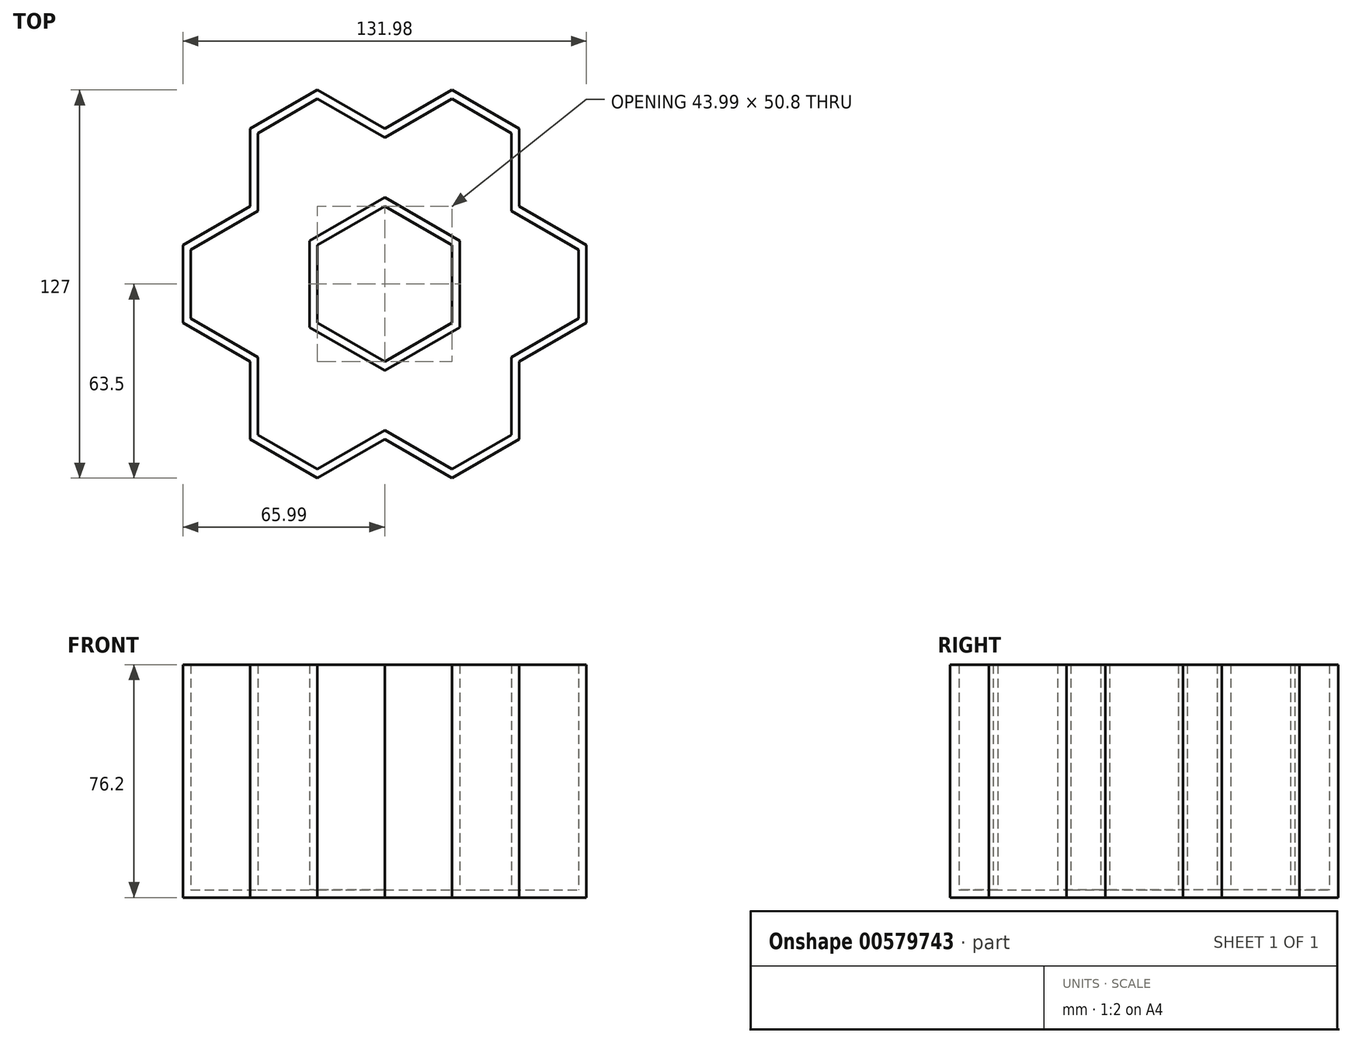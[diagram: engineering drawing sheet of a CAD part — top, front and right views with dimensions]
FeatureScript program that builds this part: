
annotation { "Feature Type Name" : "Feature", "Feature Type Description" : "" }
export const myFeature = defineFeature(function(context is Context, id is Id, definition is map)
    precondition{}
    {
        {
            var Q0;
            Q0=qCreatedBy(makeId("Top.planeOp"),FACE);
            var sketch = newSketch(context, id + "F0", { "sketchPlane" : qUnion([Q0])});
            skCircle(sketch, "E0.cCircle", {"center": v(0, 0) * mm, "radius": 25.4 * mm, "construction": true});
            skLineSegment(sketch, "E0.0", {"start": v(22, 12.7) * mm, "end": v(22, -12.7) * mm});
            skLineSegment(sketch, "E0.1", {"start": v(22, -12.7) * mm, "end": v(0, -25.4) * mm});
            skLineSegment(sketch, "E0.2", {"start": v(0, -25.4) * mm, "end": v(-22, -12.7) * mm});
            skLineSegment(sketch, "E0.3", {"start": v(-22, -12.7) * mm, "end": v(-22, 12.7) * mm});
            skLineSegment(sketch, "E0.4", {"start": v(-22, 12.7) * mm, "end": v(0, 25.4) * mm});
            skLineSegment(sketch, "E0.5", {"start": v(0, 25.4) * mm, "end": v(22, 12.7) * mm});
            skCircle(sketch, "E1.cCircle", {"center": v(44, 0) * mm, "radius": 25.4 * mm, "construction": true});
            skLineSegment(sketch, "E1.0", {"start": v(22, -12.7) * mm, "end": v(22, 12.7) * mm});
            skLineSegment(sketch, "E1.1", {"start": v(22, 12.7) * mm, "end": v(44, 25.4) * mm});
            skLineSegment(sketch, "E1.2", {"start": v(44, 25.4) * mm, "end": v(66, 12.7) * mm});
            skLineSegment(sketch, "E1.3", {"start": v(66, 12.7) * mm, "end": v(66, -12.7) * mm});
            skLineSegment(sketch, "E1.4", {"start": v(66, -12.7) * mm, "end": v(44, -25.4) * mm});
            skLineSegment(sketch, "E1.5", {"start": v(44, -25.4) * mm, "end": v(22, -12.7) * mm});
            skCircle(sketch, "E2.cCircle", {"center": v(-44, 0) * mm, "radius": 25.4 * mm, "construction": true});
            skLineSegment(sketch, "E2.0", {"start": v(-22, -12.7) * mm, "end": v(-44, -25.4) * mm});
            skLineSegment(sketch, "E2.1", {"start": v(-44, -25.4) * mm, "end": v(-66, -12.7) * mm});
            skLineSegment(sketch, "E2.2", {"start": v(-66, -12.7) * mm, "end": v(-66, 12.7) * mm});
            skLineSegment(sketch, "E2.3", {"start": v(-66, 12.7) * mm, "end": v(-44, 25.4) * mm});
            skLineSegment(sketch, "E2.4", {"start": v(-44, 25.4) * mm, "end": v(-22, 12.7) * mm});
            skLineSegment(sketch, "E2.5", {"start": v(-22, 12.7) * mm, "end": v(-22, -12.7) * mm});
            skCircle(sketch, "E3.cCircle", {"center": v(-22, 38.1) * mm, "radius": 25.4 * mm, "construction": true});
            skLineSegment(sketch, "E3.0", {"start": v(-22, 12.7) * mm, "end": v(-44, 25.4) * mm});
            skLineSegment(sketch, "E3.1", {"start": v(-44, 25.4) * mm, "end": v(-44, 50.8) * mm});
            skLineSegment(sketch, "E3.2", {"start": v(-44, 50.8) * mm, "end": v(-22, 63.5) * mm});
            skLineSegment(sketch, "E3.3", {"start": v(-22, 63.5) * mm, "end": v(0, 50.8) * mm});
            skLineSegment(sketch, "E3.4", {"start": v(0, 50.8) * mm, "end": v(0, 25.4) * mm});
            skLineSegment(sketch, "E3.5", {"start": v(0, 25.4) * mm, "end": v(-22, 12.7) * mm});
            skCircle(sketch, "E4.cCircle", {"center": v(22, 38.1) * mm, "radius": 25.4 * mm, "construction": true});
            skPoint(sketch, "E4.cCircle.centerSnap0", {"position": v(22, 0) * mm});
            skLineSegment(sketch, "E4.0", {"start": v(44, 50.8) * mm, "end": v(44, 25.4) * mm});
            skLineSegment(sketch, "E4.1", {"start": v(44, 25.4) * mm, "end": v(22, 12.7) * mm});
            skLineSegment(sketch, "E4.2", {"start": v(22, 12.7) * mm, "end": v(0, 25.4) * mm});
            skLineSegment(sketch, "E4.3", {"start": v(0, 25.4) * mm, "end": v(0, 50.8) * mm});
            skLineSegment(sketch, "E4.4", {"start": v(0, 50.8) * mm, "end": v(22, 63.5) * mm});
            skLineSegment(sketch, "E4.5", {"start": v(22, 63.5) * mm, "end": v(44, 50.8) * mm});
            skCircle(sketch, "E5.cCircle", {"center": v(-22, -38.1) * mm, "radius": 25.4 * mm, "construction": true});
            skLineSegment(sketch, "E5.0", {"start": v(0, -25.4) * mm, "end": v(0, -50.8) * mm});
            skLineSegment(sketch, "E5.1", {"start": v(0, -50.8) * mm, "end": v(-22, -63.5) * mm});
            skLineSegment(sketch, "E5.2", {"start": v(-22, -63.5) * mm, "end": v(-44, -50.8) * mm});
            skLineSegment(sketch, "E5.3", {"start": v(-44, -50.8) * mm, "end": v(-44, -25.4) * mm});
            skLineSegment(sketch, "E5.4", {"start": v(-44, -25.4) * mm, "end": v(-22, -12.7) * mm});
            skLineSegment(sketch, "E5.5", {"start": v(-22, -12.7) * mm, "end": v(0, -25.4) * mm});
            skCircle(sketch, "E6.cCircle", {"center": v(22, -38.1) * mm, "radius": 25.4 * mm, "construction": true});
            skPoint(sketch, "E6.cCircle.centerSnap0", {"position": v(0, -38.1) * mm});
            skLineSegment(sketch, "E6.0", {"start": v(44, -25.4) * mm, "end": v(44, -50.8) * mm});
            skLineSegment(sketch, "E6.1", {"start": v(44, -50.8) * mm, "end": v(22, -63.5) * mm});
            skLineSegment(sketch, "E6.2", {"start": v(22, -63.5) * mm, "end": v(0, -50.8) * mm});
            skLineSegment(sketch, "E6.3", {"start": v(0, -50.8) * mm, "end": v(0, -25.4) * mm});
            skLineSegment(sketch, "E6.4", {"start": v(0, -25.4) * mm, "end": v(22, -12.7) * mm});
            skLineSegment(sketch, "E6.5", {"start": v(22, -12.7) * mm, "end": v(44, -25.4) * mm});
            skSolve(sketch);
        }
        {
            var Q0;
            Q0 = qSketchRegion(id + "F0", true);
            var Q1;
            Q1=makeQuery(id+"F0.imprint","IMPRINT",FACE,{"disambiguationData":[TD([[makeQuery(id+"F0.imprint","IMPRINT",EDGE,{"derivedFrom":sQuery(id+"F0.wireOp",EDGE,"E1.0")}),1.0]])]});
            extrude(context, id + "F1", {"entities" : qUnion([Q0, Q1]), "depth" : 76.2 * mm, "offsetDistance" : 25.4 * mm});
        }
        {
            var Q0;
            Q0=makeQuery(id+"F1.opExtrude","CAP_FACE",FACE,{"disambiguationData":[OSD([sQuery(id+"F0.wireOp",EDGE,"E1.2"),sQuery(id+"F0.wireOp",EDGE,"E1.3"),sQuery(id+"F0.wireOp",EDGE,"E1.4"),sQuery(id+"F0.wireOp",EDGE,"E2.1"),sQuery(id+"F0.wireOp",EDGE,"E2.2"),sQuery(id+"F0.wireOp",EDGE,"E2.3"),sQuery(id+"F0.wireOp",EDGE,"E3.1"),sQuery(id+"F0.wireOp",EDGE,"E3.2"),sQuery(id+"F0.wireOp",EDGE,"E3.3"),sQuery(id+"F0.wireOp",EDGE,"E4.0"),sQuery(id+"F0.wireOp",EDGE,"E4.4"),sQuery(id+"F0.wireOp",EDGE,"E4.5"),sQuery(id+"F0.wireOp",EDGE,"E5.1"),sQuery(id+"F0.wireOp",EDGE,"E5.2"),sQuery(id+"F0.wireOp",EDGE,"E5.3"),sQuery(id+"F0.wireOp",EDGE,"E6.0"),sQuery(id+"F0.wireOp",EDGE,"E6.1"),sQuery(id+"F0.wireOp",EDGE,"E6.2")])],"isStart":false});
            shell(context, id + "F2", {"entities" : qUnion([Q0]), "thickness" : 2.54 * mm});
        }
    });
